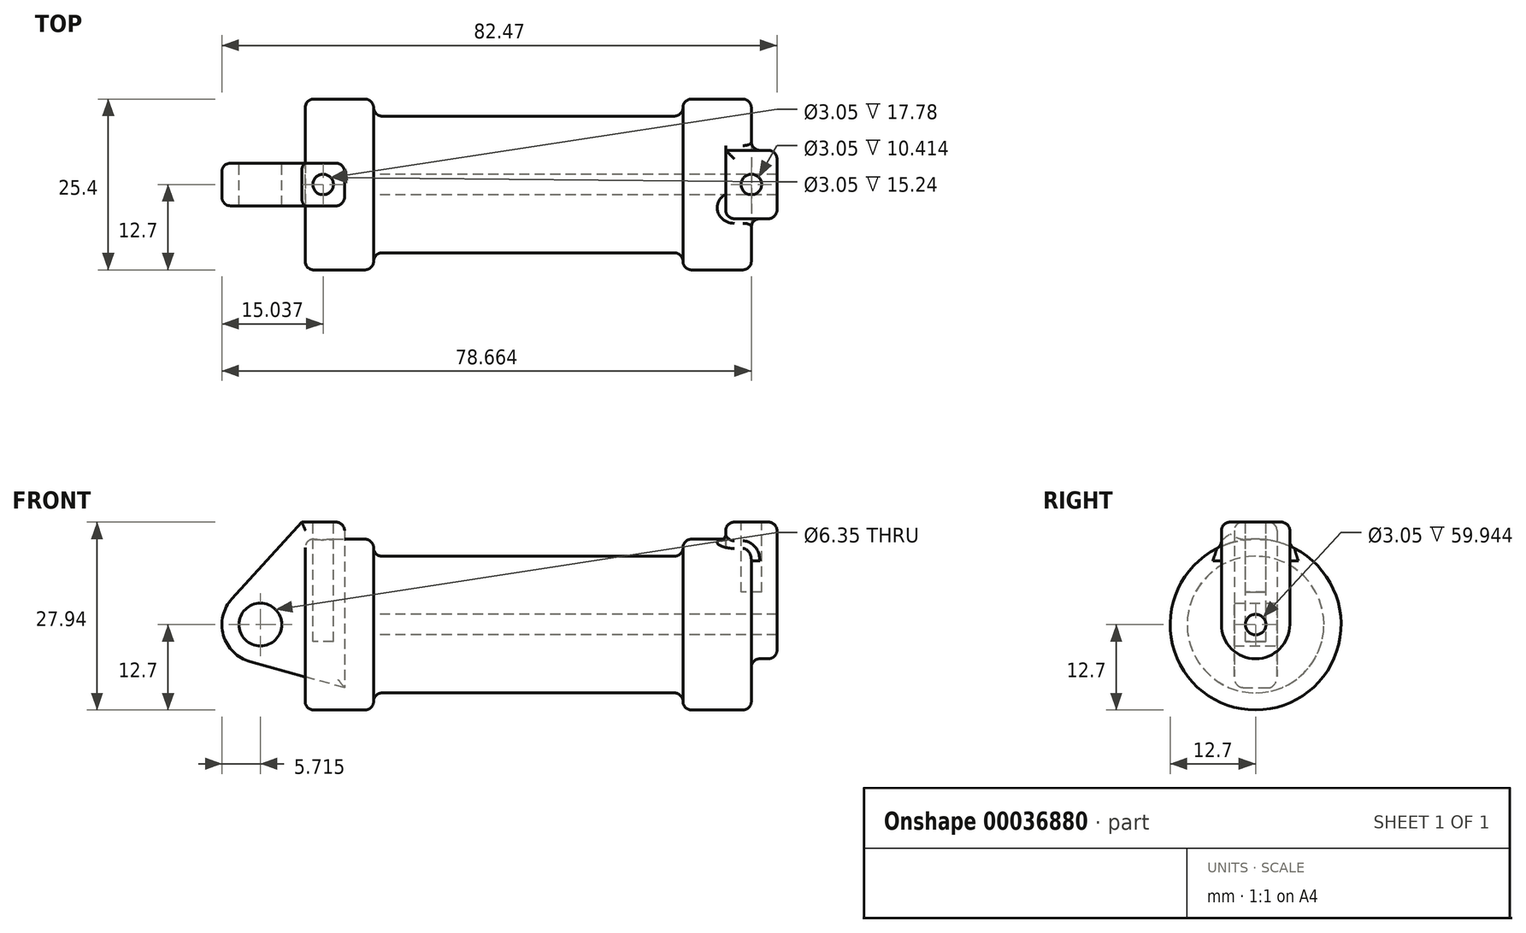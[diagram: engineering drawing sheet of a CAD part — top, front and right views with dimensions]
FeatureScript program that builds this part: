
annotation { "Feature Type Name" : "Feature", "Feature Type Description" : "" }
export const myFeature = defineFeature(function(context is Context, id is Id, definition is map)
    precondition{}
    {
        {
            var Q0;
            Q0=qCreatedBy(makeId("Front.planeOp"),FACE);
            var sketch = newSketch(context, id + "F0", { "sketchPlane" : qUnion([Q0])});
            skLineSegment(sketch, "E0", {"start": v(0, 0) * mm, "end": v(0, 12.7) * mm});
            skLineSegment(sketch, "E1", {"start": v(0, 12.7) * mm, "end": v(10.16, 12.7) * mm});
            skLineSegment(sketch, "E2", {"start": v(10.16, 12.7) * mm, "end": v(10.16, 10.16) * mm});
            skLineSegment(sketch, "E3", {"start": v(10.16, 10.16) * mm, "end": v(56.13, 10.16) * mm});
            skLineSegment(sketch, "E4", {"start": v(56.13, 10.16) * mm, "end": v(56.13, 12.7) * mm});
            skLineSegment(sketch, "E5", {"start": v(56.13, 12.7) * mm, "end": v(66.3, 12.7) * mm});
            skLineSegment(sketch, "E6", {"start": v(66.3, 12.7) * mm, "end": v(66.3, 0) * mm});
            skLineSegment(sketch, "E7", {"start": v(66.3, 0) * mm, "end": v(0, 0) * mm});
            skLineSegment(sketch, "E8", {"start": v(5.84, 15.24) * mm, "end": v(-0.5, 15.24) * mm});
            skLineSegment(sketch, "E9", {"start": v(-0.5, 15.24) * mm, "end": v(-10.88, 3.85) * mm});
            skLineSegment(sketch, "E10", {"start": v(0, 0) * mm, "end": v(-6.65, 0) * mm});
            skCircle(sketch, "E11", {"center": v(-6.65, 0) * mm, "radius": 5.72 * mm});
            skCircle(sketch, "E12", {"center": v(-6.65, 0) * mm, "radius": 3.18 * mm});
            skLineSegment(sketch, "E13", {"start": v(5.84, 15.24) * mm, "end": v(5.84, -9.4) * mm});
            skLineSegment(sketch, "E14", {"start": v(5.84, -9.4) * mm, "end": v(-8.18, -5.5) * mm});
            skLineSegment(sketch, "E15", {"start": v(0, 0) * mm, "end": v(0, -7.78) * mm});
            skSolve(sketch);
        }
        {
            var Q0;
            {var subQ5=sQuery(id+"F0.wireOp",EDGE,"E0");Q0=makeQuery(id+"F0.imprint","IMPRINT",FACE,{"disambiguationData":[TD([[makeQuery(id+"F0.imprint","IMPRINT",EDGE,{"derivedFrom":subQ5}),-1.0]])]});}
            var Q1;
            Q1=sQuery(id+"F0.wireOp",EDGE,"E7");
            revolve(context, id + "F1", {"entities" : qUnion([Q0]), "axis" : qUnion([Q1]), "revolveType" : RevolveType.FULL});
        }
        {
            var Q0;
            {var subQ6=sQuery(id+"F0.wireOp",EDGE,"E2");Q0=makeQuery(id+"F0.imprint","IMPRINT",FACE,{"disambiguationData":[TD([[makeQuery(id+"F0.imprint","IMPRINT",EDGE,{"derivedFrom":subQ6}),-1.0]])]});}
            var Q1;
            Q1=sQuery(id+"F0.wireOp",EDGE,"E7");
            revolve(context, id + "F2", {"operationType" : NewBodyOperationType.ADD, "entities" : qUnion([Q0]), "axis" : qUnion([Q1]), "revolveType" : RevolveType.FULL});
        }
        {
            var Q0;
            {var subQ8=sQuery(id+"F0.wireOp",EDGE,"E0");Q0=makeQuery(id+"F0.imprint","IMPRINT",FACE,{"disambiguationData":[TD([[makeQuery(id+"F0.imprint","IMPRINT",EDGE,{"derivedFrom":subQ8}),1.0]])]});}
            var Q1;
            {var subQ5=sQuery(id+"F0.wireOp",EDGE,"E0");Q1=makeQuery(id+"F0.imprint","IMPRINT",FACE,{"disambiguationData":[TD([[makeQuery(id+"F0.imprint","IMPRINT",EDGE,{"derivedFrom":subQ5}),-1.0]])]});}
            var Q2;
            {var subQ1=sQuery(id+"F0.wireOp",EDGE,"E15");Q2=makeQuery(id+"F0.imprint","IMPRINT",FACE,{"disambiguationData":[TD([[makeQuery(id+"F0.imprint","IMPRINT",EDGE,{"derivedFrom":subQ1}),1.0]])]});}
            var Q3;
            {var subQ0=sQuery(id+"F0.wireOp",EDGE,"E15");Q3=makeQuery(id+"F0.imprint","IMPRINT",FACE,{"disambiguationData":[TD([[makeQuery(id+"F0.imprint","IMPRINT",EDGE,{"derivedFrom":subQ0}),-1.0]])]});}
            var Q4;
            {var subQ0=sQuery(id+"F0.wireOp",EDGE,"E12");Q4=makeQuery(id+"F0.imprint","IMPRINT",FACE,{"disambiguationData":[TD([[makeQuery(id+"F0.imprint","IMPRINT",EDGE,{"derivedFrom":subQ0}),-1.0]])]});}
            extrude(context, id + "F3", {"entities" : qUnion([Q0, Q1, Q2, Q3, Q4]), "endBound" : BoundingType.SYMMETRIC, "depth" : 6.35 * mm});
        }
        {
            var Q0;
            Q0=makeQuery(id+"F2.opRevolve","SWEPT_FACE",FACE,{"disambiguationData":[OSD([sQuery(id+"F0.wireOp",EDGE,"E6")])]});
            var sketch = newSketch(context, id + "F4", { "sketchPlane" : qUnion([Q0])});
            skCircle(sketch, "E16", {"center": v(0, 0) * mm, "radius": 5.08 * mm});
            skCircle(sketch, "E17", {"center": v(0, 0) * mm, "radius": 1.52 * mm});
            skLineSegment(sketch, "E18", {"start": v(-5.08, 0) * mm, "end": v(-5.08, 15.24) * mm});
            skLineSegment(sketch, "E19", {"start": v(5.08, 0) * mm, "end": v(5.08, 15.24) * mm});
            skLineSegment(sketch, "E20", {"start": v(-5.08, 15.24) * mm, "end": v(5.08, 15.24) * mm});
            skSolve(sketch);
        }
        {
            var Q0;
            {var subQ5=sQuery(id+"F4.wireOp",EDGE,"E20");Q0=makeQuery(id+"F4.imprint","IMPRINT",FACE,{"disambiguationData":[TD([[makeQuery(id+"F4.imprint","IMPRINT",EDGE,{"derivedFrom":subQ5}),-1.0]])]});}
            var Q1;
            {var subQ3=sQuery(id+"F4.wireOp",EDGE,"E18");var subQ5=sQuery(id+"F4.wireOp",EDGE,"E16");var subQ7=makeQuery(id+"F4.imprint","INTERSECT",VERTEX,{"derivedFrom":[subQ5,subQ3]});Q1=makeQuery(id+"F4.imprint","IMPRINT",FACE,{"disambiguationData":[TD([[makeQuery(id+"F4.imprint","IMPRINT",EDGE,{"disambiguationData":[TD([[subQ7,1.0]])],"derivedFrom":subQ5}),-1.0]])]});}
            var Q2;
            Q2=makeQuery(id+"F4.imprint","IMPRINT",FACE,{"disambiguationData":[TD([[makeQuery(id+"F4.imprint","IMPRINT",EDGE,{"derivedFrom":sQuery(id+"F4.wireOp",EDGE,"E17")}),-1.0]])]});
            extrude(context, id + "F5", {"entities" : qUnion([Q0, Q1, Q2]), "operationType" : NewBodyOperationType.ADD, "endBound" : BoundingType.SYMMETRIC, "depth" : 7.62 * mm});
        }
        {
            var Q0;
            Q0=makeQuery(id+"F5.boolean.opBoolean","SPLIT",FACE,{"disambiguationData":[TD([makeQuery(id+"F5.opExtrude","SWEPT_FACE",FACE,{"disambiguationData":[OSD([sQuery(id+"F4.wireOp",EDGE,"E17")])]})])],"derivedFrom":makeQuery(id+"F2.opRevolve","SWEPT_FACE",FACE,{"disambiguationData":[OSD([sQuery(id+"F0.wireOp",EDGE,"E6")])]})});
            var Q1;
            Q1=makeQuery(id+"F2.opRevolve","SWEPT_FACE",FACE,{"disambiguationData":[OSD([sQuery(id+"F0.wireOp",EDGE,"E2")])]});
            extrude(context, id + "F6", {"entities" : qUnion([Q0]), "operationType" : NewBodyOperationType.REMOVE, "endBound" : BoundingType.UP_TO_SURFACE, "oppositeDirection" : true, "endBoundEntityFace" : qUnion([Q1]), "depth" : 25.4 * mm});
        }
        {
            var Q0;
            Q0=makeQuery(id+"F5.opExtrude","SWEPT_FACE",FACE,{"disambiguationData":[OSD([sQuery(id+"F4.wireOp",EDGE,"E20")])]});
            var sketch = newSketch(context, id + "F7", { "sketchPlane" : qUnion([Q0])});
            skCircle(sketch, "E21", {"center": v(66.3, 0) * mm, "radius": 1.52 * mm});
            skPoint(sketch, "E21.centerSnap0", {"position": v(62.48, 0) * mm});
            skPoint(sketch, "E21.centerSnap1", {"position": v(66.3, -5.08) * mm});
            skSolve(sketch);
        }
        {
            var Q0;
            Q0=makeQuery(id+"F3.opExtrude","SWEPT_FACE",FACE,{"disambiguationData":[OSD([sQuery(id+"F0.wireOp",EDGE,"E8")])]});
            var sketch = newSketch(context, id + "F8", { "sketchPlane" : qUnion([Q0])});
            skCircle(sketch, "E22", {"center": v(2.67, 0) * mm, "radius": 1.52 * mm});
            skPoint(sketch, "E22.centerSnap0", {"position": v(5.84, 0) * mm});
            skPoint(sketch, "E22.centerSnap1", {"position": v(2.67, -3.18) * mm});
            skSolve(sketch);
        }
        {
            var Q0;
            Q0=makeQuery(id+"F7.imprint","IMPRINT",FACE,{"disambiguationData":[TD([[makeQuery(id+"F7.imprint","IMPRINT",EDGE,{"derivedFrom":sQuery(id+"F7.wireOp",EDGE,"E21")}),1.0]])]});
            extrude(context, id + "F9", {"entities" : qUnion([Q0]), "operationType" : NewBodyOperationType.REMOVE, "oppositeDirection" : true, "depth" : 10.4 * mm});
        }
        {
            var Q0;
            Q0=makeQuery(id+"F8.imprint","IMPRINT",FACE,{"disambiguationData":[TD([[makeQuery(id+"F8.imprint","IMPRINT",EDGE,{"derivedFrom":sQuery(id+"F8.wireOp",EDGE,"E22")}),1.0]])]});
            extrude(context, id + "F10", {"entities" : qUnion([Q0]), "operationType" : NewBodyOperationType.REMOVE, "oppositeDirection" : true, "depth" : 17.78 * mm});
        }
        {
            var Q0;
            Q0=makeQuery(id+"F5.opExtrude","CAP_EDGE",EDGE,{"disambiguationData":[OSD([sQuery(id+"F4.wireOp",EDGE,"E18")])],"isStart":false});
            var Q1;
            Q1=makeQuery(id+"F5.opExtrude","SWEPT_EDGE",EDGE,{"disambiguationData":[OSD([sQuery(id+"F4.wireOp",EDGE,"E18"),sQuery(id+"F4.wireOp",EDGE,"E20")])]});
            var Q2;
            Q2=makeQuery(id+"F5.opExtrude","CAP_EDGE",EDGE,{"disambiguationData":[OSD([sQuery(id+"F4.wireOp",EDGE,"E20")])],"isStart":true});
            var Q3;
            Q3=makeQuery(id+"F5.opExtrude","CAP_EDGE",EDGE,{"disambiguationData":[OSD([sQuery(id+"F4.wireOp",EDGE,"E20")])],"isStart":false});
            var Q4;
            Q4=makeQuery(id+"F5.opExtrude","SWEPT_EDGE",EDGE,{"disambiguationData":[OSD([sQuery(id+"F4.wireOp",EDGE,"E19"),sQuery(id+"F4.wireOp",EDGE,"E20")])]});
            var Q5;
            Q5=makeQuery(id+"F5.opExtrude","CAP_EDGE",EDGE,{"disambiguationData":[OSD([sQuery(id+"F4.wireOp",EDGE,"E19")])],"isStart":false});
            var Q6;
            Q6=makeQuery(id+"F5.opExtrude","CAP_EDGE",EDGE,{"disambiguationData":[OSD([sQuery(id+"F4.wireOp",EDGE,"E16")])],"isStart":false});
            var Q7;
            Q7=makeQuery(id+"F5.boolean.opBoolean","INTERSECT",EDGE,{"derivedFrom":[makeQuery(id+"F2.opRevolve","SWEPT_FACE",FACE,{"disambiguationData":[OSD([sQuery(id+"F0.wireOp",EDGE,"E6")])]}),makeQuery(id+"F5.opExtrude","SWEPT_FACE",FACE,{"disambiguationData":[OSD([sQuery(id+"F4.wireOp",EDGE,"E16")])]})]});
            var Q8;
            Q8=makeQuery(id+"F5.boolean.opBoolean","INTERSECT",EDGE,{"derivedFrom":[makeQuery(id+"F2.opRevolve","SWEPT_FACE",FACE,{"disambiguationData":[OSD([sQuery(id+"F0.wireOp",EDGE,"E6")])]}),makeQuery(id+"F5.opExtrude","SWEPT_FACE",FACE,{"disambiguationData":[OSD([sQuery(id+"F4.wireOp",EDGE,"E18")])]})]});
            var Q9;
            Q9=makeQuery(id+"F5.opExtrude","CAP_EDGE",EDGE,{"disambiguationData":[OSD([sQuery(id+"F4.wireOp",EDGE,"E18")])],"isStart":true});
            var Q10;
            Q10=makeQuery(id+"F5.boolean.opBoolean","INTERSECT",EDGE,{"derivedFrom":[makeQuery(id+"F2.opRevolve","SWEPT_FACE",FACE,{"disambiguationData":[OSD([sQuery(id+"F0.wireOp",EDGE,"E5")])]}),makeQuery(id+"F5.opExtrude","SWEPT_FACE",FACE,{"disambiguationData":[OSD([sQuery(id+"F4.wireOp",EDGE,"E18")])]})]});
            var Q11;
            Q11=makeQuery(id+"F5.boolean.opBoolean","INTERSECT",EDGE,{"derivedFrom":[makeQuery(id+"F2.opRevolve","SWEPT_FACE",FACE,{"disambiguationData":[OSD([sQuery(id+"F0.wireOp",EDGE,"E6")])]}),makeQuery(id+"F5.opExtrude","SWEPT_FACE",FACE,{"disambiguationData":[OSD([sQuery(id+"F4.wireOp",EDGE,"E19")])]})]});
            var Q12;
            Q12=makeQuery(id+"F5.boolean.opBoolean","INTERSECT",EDGE,{"derivedFrom":[makeQuery(id+"F2.opRevolve","SWEPT_FACE",FACE,{"disambiguationData":[OSD([sQuery(id+"F0.wireOp",EDGE,"E5")])]}),makeQuery(id+"F5.opExtrude","SWEPT_FACE",FACE,{"disambiguationData":[OSD([sQuery(id+"F4.wireOp",EDGE,"E19")])]})]});
            var Q13;
            Q13=makeQuery(id+"F2.opRevolve","SWEPT_EDGE",EDGE,{"disambiguationData":[OSD([sQuery(id+"F0.wireOp",EDGE,"E5"),sQuery(id+"F0.wireOp",EDGE,"E6")])]});
            var Q14;
            Q14=makeQuery(id+"F2.opRevolve","SWEPT_EDGE",EDGE,{"disambiguationData":[OSD([sQuery(id+"F0.wireOp",EDGE,"E4"),sQuery(id+"F0.wireOp",EDGE,"E5")])]});
            var Q15;
            Q15=makeQuery(id+"F2.opRevolve","SWEPT_EDGE",EDGE,{"disambiguationData":[OSD([sQuery(id+"F0.wireOp",EDGE,"E1"),sQuery(id+"F0.wireOp",EDGE,"E2")])]});
            var Q16;
            Q16=makeQuery(id+"F2.opRevolve","SWEPT_EDGE",EDGE,{"disambiguationData":[OSD([sQuery(id+"F0.wireOp",EDGE,"E2"),sQuery(id+"F0.wireOp",EDGE,"E3")])]});
            var Q17;
            Q17=makeQuery(id+"F1.opRevolve","SWEPT_EDGE",EDGE,{"disambiguationData":[OSD([sQuery(id+"F0.wireOp",EDGE,"E0"),sQuery(id+"F0.wireOp",EDGE,"E1")])]});
            var Q18;
            Q18=makeQuery(id+"F3.opExtrude","CAP_EDGE",EDGE,{"disambiguationData":[OSD([sQuery(id+"F0.wireOp",EDGE,"E8")])],"isStart":true});
            var Q19;
            Q19=makeQuery(id+"F3.opExtrude","SWEPT_EDGE",EDGE,{"disambiguationData":[OSD([sQuery(id+"F0.wireOp",EDGE,"E8"),sQuery(id+"F0.wireOp",EDGE,"E13")])]});
            var Q20;
            Q20=makeQuery(id+"F3.opExtrude","CAP_EDGE",EDGE,{"disambiguationData":[OSD([sQuery(id+"F0.wireOp",EDGE,"E9")])],"isStart":true});
            var Q21;
            Q21=makeQuery(id+"F3.opExtrude","CAP_EDGE",EDGE,{"disambiguationData":[OSD([sQuery(id+"F0.wireOp",EDGE,"E13")])],"isStart":true});
            var Q22;
            Q22=makeQuery(id+"F3.opExtrude","CAP_EDGE",EDGE,{"disambiguationData":[OSD([sQuery(id+"F0.wireOp",EDGE,"E13")])],"isStart":false});
            var Q23;
            Q23=makeQuery(id+"F3.opExtrude","CAP_EDGE",EDGE,{"disambiguationData":[OSD([sQuery(id+"F0.wireOp",EDGE,"E8")])],"isStart":false});
            var Q24;
            Q24=makeQuery(id+"F3.opExtrude","CAP_EDGE",EDGE,{"disambiguationData":[OSD([sQuery(id+"F0.wireOp",EDGE,"E9")])],"isStart":false});
            var Q25;
            Q25=makeQuery(id+"F3.opExtrude","CAP_EDGE",EDGE,{"disambiguationData":[OSD([sQuery(id+"F0.wireOp",EDGE,"E11")])],"isStart":false});
            var Q26;
            Q26=makeQuery(id+"F3.opExtrude","CAP_EDGE",EDGE,{"disambiguationData":[OSD([sQuery(id+"F0.wireOp",EDGE,"E11")])],"isStart":true});
            var Q27;
            Q27=makeQuery(id+"F3.opExtrude","CAP_EDGE",EDGE,{"disambiguationData":[OSD([sQuery(id+"F0.wireOp",EDGE,"E14")])],"isStart":false});
            var Q28;
            Q28=makeQuery(id+"F3.opExtrude","CAP_EDGE",EDGE,{"disambiguationData":[OSD([sQuery(id+"F0.wireOp",EDGE,"E14")])],"isStart":true});
            var Q29;
            Q29=makeQuery(id+"F2.opRevolve","SWEPT_EDGE",EDGE,{"disambiguationData":[OSD([sQuery(id+"F0.wireOp",EDGE,"E3"),sQuery(id+"F0.wireOp",EDGE,"E4")])]});
            fillet(context, id + "F11", {"entities" : qUnion([Q0, Q1, Q2, Q3, Q4, Q5, Q6, Q7, Q8, Q9, Q10, Q11, Q12, Q13, Q14, Q15, Q16, Q17, Q18, Q19, Q20, Q21, Q22, Q23, Q24, Q25, Q26, Q27, Q28, Q29]), "radius" : 1.27 * mm, "tangentPropagation" : true, "allowEdgeOverflow" : false});
        }
    });
